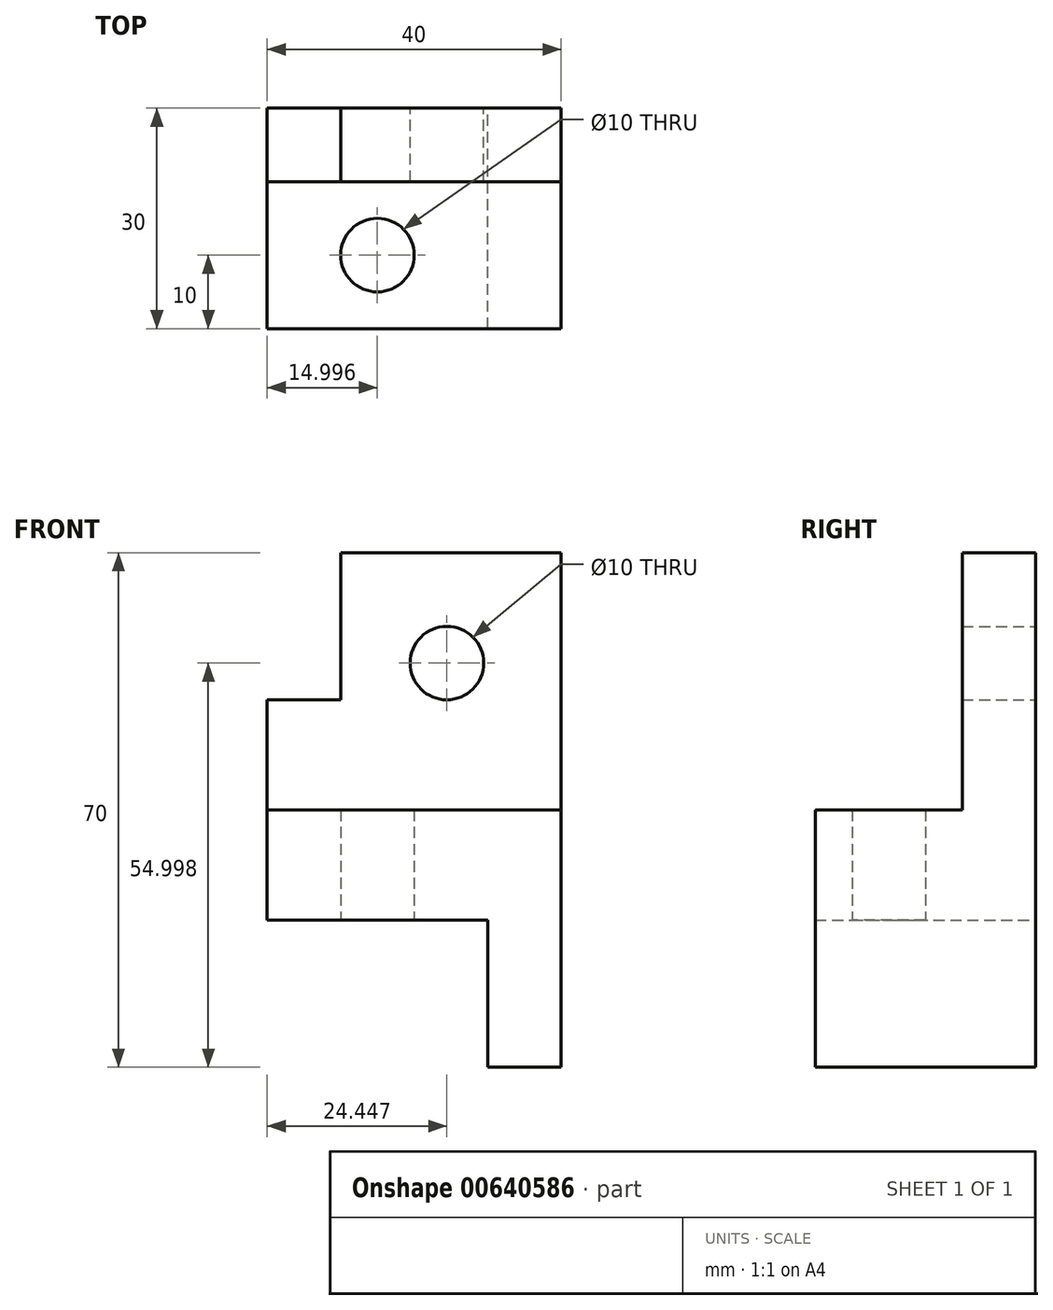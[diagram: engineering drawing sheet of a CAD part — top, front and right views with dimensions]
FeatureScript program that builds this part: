
annotation { "Feature Type Name" : "Feature", "Feature Type Description" : "" }
export const myFeature = defineFeature(function(context is Context, id is Id, definition is map)
    precondition{}
    {
        {
            var Q0;
            Q0=qCreatedBy(makeId("Front.planeOp"),FACE);
            var sketch = newSketch(context, id + "F0", { "sketchPlane" : qUnion([Q0])});
            skLineSegment(sketch, "E0", {"start": v(-20.03, 15.32) * mm, "end": v(-20.03, -14.68) * mm});
            skLineSegment(sketch, "E1", {"start": v(9.97, -34.68) * mm, "end": v(19.97, -34.68) * mm});
            skLineSegment(sketch, "E2", {"start": v(19.97, -34.68) * mm, "end": v(19.97, 35.32) * mm});
            skLineSegment(sketch, "E3", {"start": v(19.97, 35.32) * mm, "end": v(-10.03, 35.32) * mm});
            skLineSegment(sketch, "E4", {"start": v(-20.03, -14.68) * mm, "end": v(9.97, -14.68) * mm});
            skLineSegment(sketch, "E5", {"start": v(-20.03, 0.32) * mm, "end": v(19.97, 0.32) * mm});
            skLineSegment(sketch, "E6", {"start": v(9.97, -14.68) * mm, "end": v(9.97, -34.68) * mm});
            skLineSegment(sketch, "E7", {"start": v(-20.03, 15.32) * mm, "end": v(-10.03, 15.32) * mm});
            skLineSegment(sketch, "E8", {"start": v(-10.03, 15.32) * mm, "end": v(-10.03, 35.32) * mm});
            skCircle(sketch, "E9", {"center": v(4.42, 20.32) * mm, "radius": 5 * mm});
            skSolve(sketch);
        }
        {
            var Q0;
            Q0 = qSketchRegion(id + "F0", true);
            extrude(context, id + "F1", {"entities" : qUnion([Q0]), "depth" : 10 * mm, "offsetDistance" : 25 * mm});
        }
        {
            var Q0;
            {var subQ1=sQuery(id+"F0.wireOp",EDGE,"E1");Q0=makeQuery(id+"F0.imprint","IMPRINT",FACE,{"disambiguationData":[TD([[makeQuery(id+"F0.imprint","IMPRINT",EDGE,{"derivedFrom":subQ1}),1.0]])]});}
            var Q1;
            Q1 = qSketchRegion(id + "F3", true);
            extrude(context, id + "F2", {"entities" : qUnion([Q0, Q1]), "operationType" : NewBodyOperationType.ADD, "depth" : 30 * mm, "offsetDistance" : 25 * mm});
        }
        {
            var Q0;
            {var subQ0=sQuery(id+"F0.wireOp",EDGE,"E4");Q0=makeQuery(id+"F2.boolean.opBoolean","MERGE",FACE,{"derivedFrom":[makeQuery(id+"F1.opExtrude","SWEPT_FACE",FACE,{"disambiguationData":[OSD([subQ0])]}),makeQuery(id+"F2.opExtrude","SWEPT_FACE",FACE,{"disambiguationData":[OSD([subQ0])]})]});}
            var sketch = newSketch(context, id + "F3", { "sketchPlane" : qUnion([Q0])});
            skCircle(sketch, "E10", {"center": v(-5.03, 20) * mm, "radius": 5 * mm});
            skSolve(sketch);
        }
        {
            var Q0;
            Q0=makeQuery(id+"F3.imprint","IMPRINT",FACE,{"disambiguationData":[TD([[makeQuery(id+"F3.imprint","IMPRINT",EDGE,{"derivedFrom":sQuery(id+"F3.wireOp",EDGE,"E10")}),1.0]])]});
            extrude(context, id + "F4", {"entities" : qUnion([Q0]), "operationType" : NewBodyOperationType.REMOVE, "oppositeDirection" : true, "depth" : 25 * mm, "offsetDistance" : 25 * mm});
        }
    });
